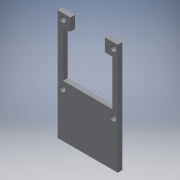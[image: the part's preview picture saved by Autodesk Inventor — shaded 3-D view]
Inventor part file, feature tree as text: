
AUTODESK INVENTOR PART (.ipt)
format: ipt  version: 2018 (Build 220112000, 112)  size: 179,712 bytes
history: native  units: mm
features: sketch x5, projected_geometry x4, extrude x3, hole x2, fillet x1
ambient origin geometry x8: Origin, YZ Plane, XZ Plane, XY Plane, X Axis, Y Axis, Z Axis, Center Point
bodies: Solid1 (feature_tree)
feature tree (15):
  extrude  "Extrusion1"  Depth=45.0mm
  extrude  "Extrusion2"  Depth=2.25mm
  hole  "Hole1"  [1 undecoded]
  hole  "Hole2"  [1 undecoded]
  fillet  "Fillet1"  Radius=14.0mm
  extrude  "Extrusion3"  Depth=18.5mm
  sketch  "Sketch1"  dims[d0=24.5mm d1=45.0mm]
  sketch  "Sketch2"  dims[d2=1.95mm d3=0.0mm d4=2.25mm]
  projected_geometry  "Projected Loop1"
  sketch  "Sketch3"  dims[d5=20.0mm d6=2.25mm]
  projected_geometry  "Projected Loop2"
  sketch  "Sketch4"  dims[d7=5.25mm d8=5.25mm d9=14.0mm]
  projected_geometry  "Projected Loop3"
  sketch  "Sketch5"  dims[d10=5.25mm d11=18.5mm d12=10.0mm d13=0.0mm d14=20.5mm d15=2.0mm d16=2.195mm d17=2.0mm d18=2.4mm d19=6.0mm d20=4.4mm d21=2.0mm d22=90.0deg d23=8.0mm d24=20.594885mm d25=20.5mm d26=26.65mm d27=2.0mm d28=2.0mm d29=2.4mm d30=6.0mm d31=4.4mm d32=2.0mm d33=90.0deg d34=8.0mm d35=20.594885mm d36=0.5mm d37=18.0mm d38=5.0mm d39=0.0mm]
  projected_geometry  "Projected Loop4"
note: 2 required parameter values undecoded (feature->parameter linkage not recoverable at this tier; creation-order binding heuristic only, values carry confidence <= 0.55)
